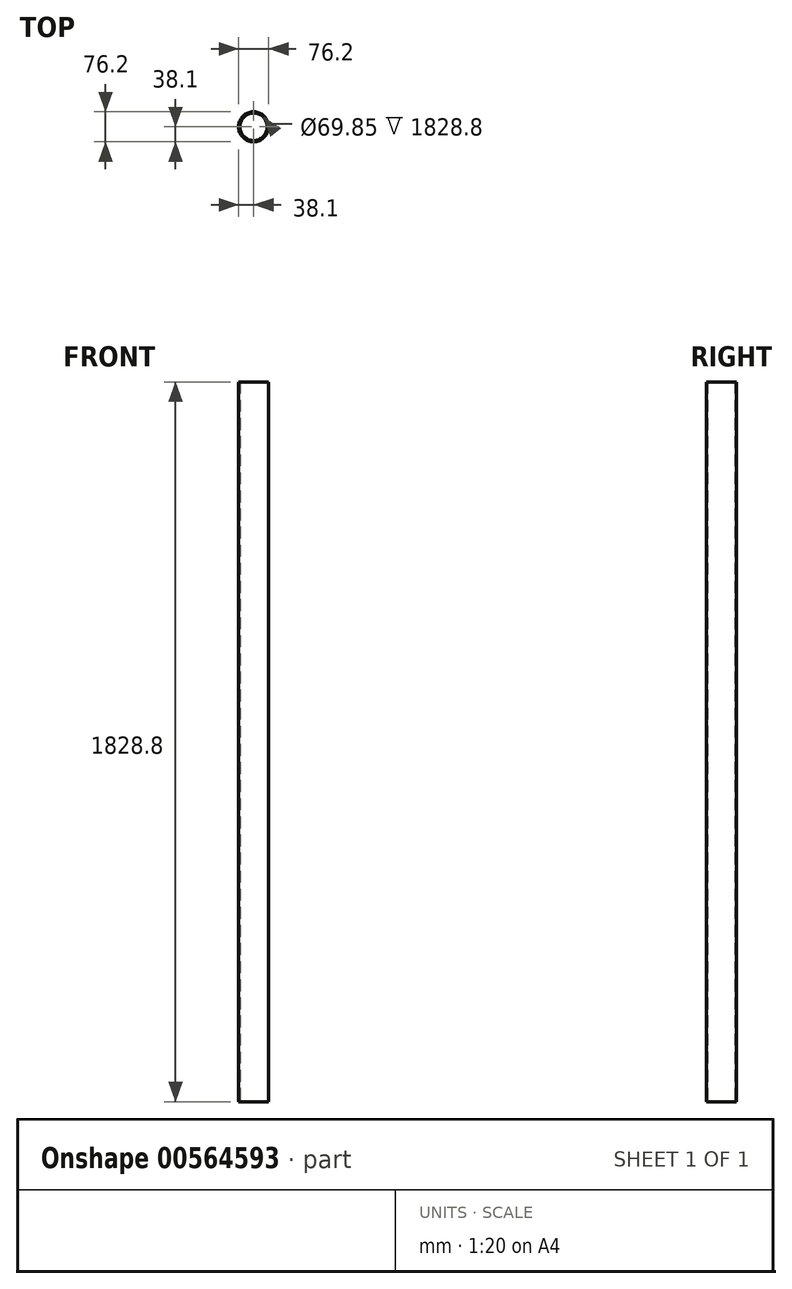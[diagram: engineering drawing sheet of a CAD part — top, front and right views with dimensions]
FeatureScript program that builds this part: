
annotation { "Feature Type Name" : "Feature", "Feature Type Description" : "" }
export const myFeature = defineFeature(function(context is Context, id is Id, definition is map)
    precondition{}
    {
        {
            var Q0;
            Q0=qCreatedBy(makeId("Top.planeOp"),FACE);
            var sketch = newSketch(context, id + "F0", { "sketchPlane" : qUnion([Q0])});
            skCircle(sketch, "E0", {"center": v(0, 11.06) * mm, "radius": 38.1 * mm});
            skCircle(sketch, "E1", {"center": v(0, 11.06) * mm, "radius": 34.93 * mm});
            skSolve(sketch);
        }
        {
            var Q0;
            Q0 = qSketchRegion(id + "F0", true);
            extrude(context, id + "F1", {"entities" : qUnion([Q0]), "depth" : 1828.8 * mm, "offsetDistance" : 25.4 * mm});
        }
    });
